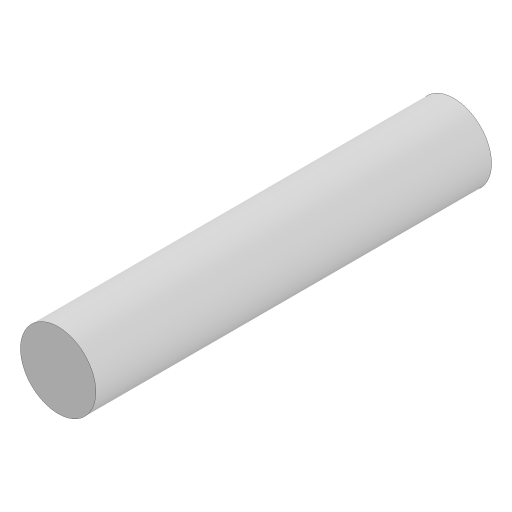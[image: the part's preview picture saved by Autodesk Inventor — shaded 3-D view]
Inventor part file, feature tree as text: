
AUTODESK INVENTOR PART (.ipt)
format: ipt  version: 2023 (Build 270158000, 158)  size: 88,064 bytes
history: native  units: mm
features: extrude x1, sketch x1
ambient origin geometry x8: Origin, YZ Plane, XZ Plane, XY Plane, X Axis, Y Axis, Z Axis, Center Point
bodies: Solid1 (feature_tree)
feature tree (2):
  extrude  "Extrusion1"  Depth=21.0mm TaperAngle=0.0deg
  sketch  "Sketch1"  dims[d0=4.0mm d1=21.0mm d2=0.0mm]
